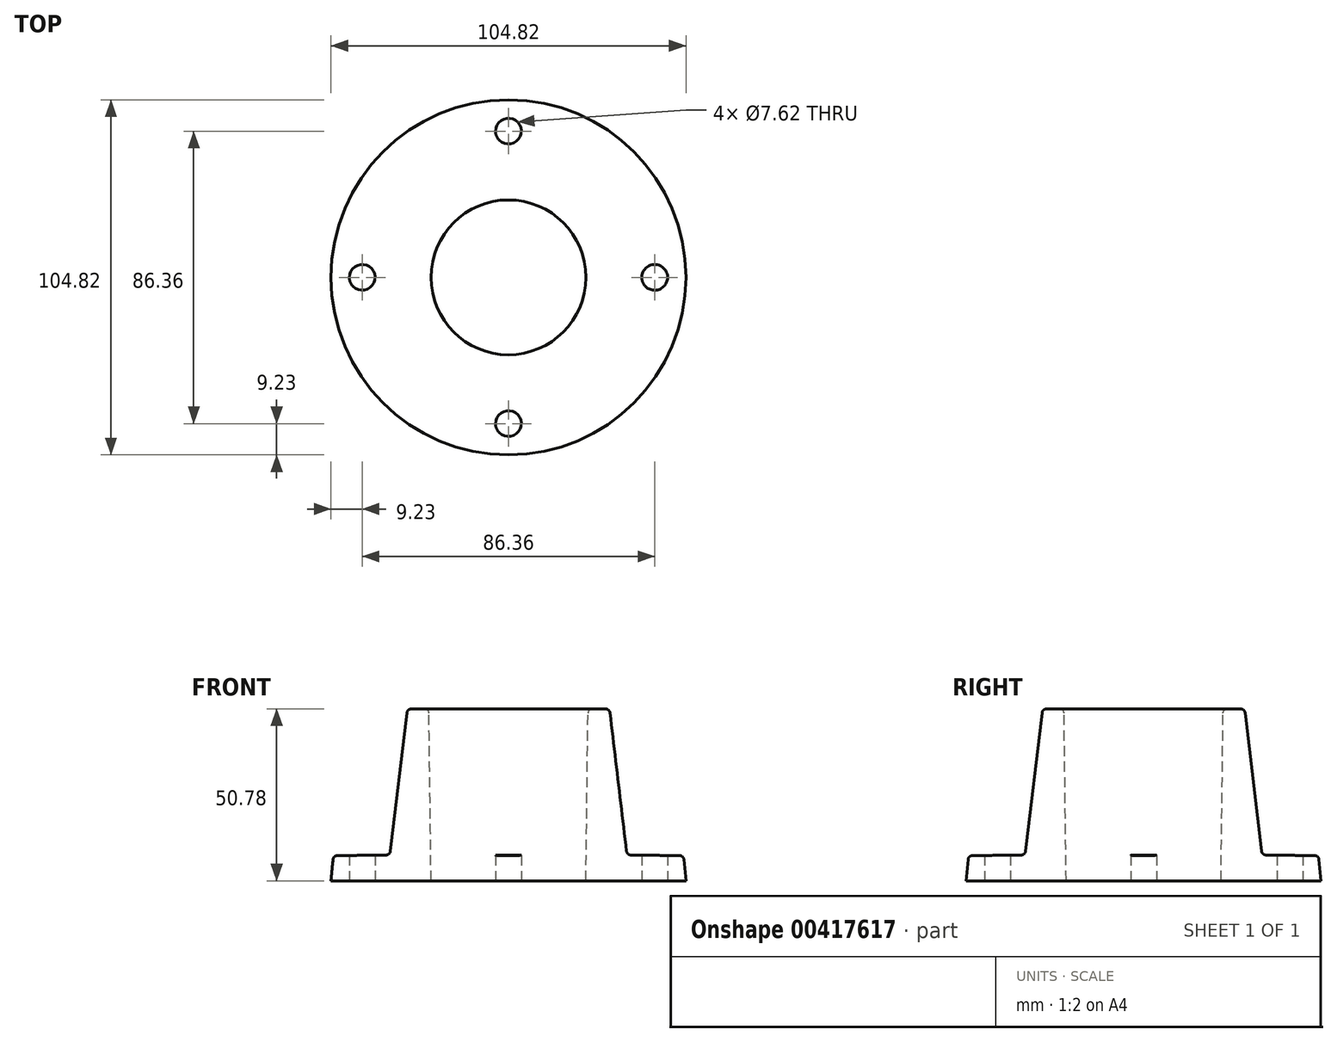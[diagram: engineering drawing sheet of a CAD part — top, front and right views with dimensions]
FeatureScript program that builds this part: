
annotation { "Feature Type Name" : "Feature", "Feature Type Description" : "" }
export const myFeature = defineFeature(function(context is Context, id is Id, definition is map)
    precondition{}
    {
        {
            var Q0;
            Q0=qCreatedBy(makeId("Front.planeOp"),FACE);
            var sketch = newSketch(context, id + "F0", { "sketchPlane" : qUnion([Q0])});
            skLineSegment(sketch, "E0", {"start": v(0, 0) * mm, "end": v(0, 50.8) * mm});
            skLineSegment(sketch, "E1", {"start": v(0, 50.8) * mm, "end": v(23.5, 50.8) * mm});
            skLineSegment(sketch, "E2", {"start": v(0, 0) * mm, "end": v(22.86, 0) * mm});
            skLineSegment(sketch, "E3", {"start": v(22.86, 0) * mm, "end": v(23.5, 50.8) * mm});
            skLineSegment(sketch, "E4", {"start": v(23.5, 50.8) * mm, "end": v(29.84, 50.72) * mm});
            skLineSegment(sketch, "E5", {"start": v(29.84, 50.72) * mm, "end": v(35.9, 0) * mm});
            skLineSegment(sketch, "E6", {"start": v(52.5, 7.41) * mm, "end": v(34.99, 7.63) * mm});
            skLineSegment(sketch, "E7", {"start": v(22.86, 0) * mm, "end": v(35.9, 0) * mm});
            skLineSegment(sketch, "E8", {"start": v(35.9, 0) * mm, "end": v(52.41, 0) * mm});
            skLineSegment(sketch, "E9", {"start": v(52.41, 0) * mm, "end": v(51.7, 7.42) * mm});
            skSolve(sketch);
        }
        {
            var Q0;
            Q0=makeQuery(id+"F0.imprint","IMPRINT",FACE,{"disambiguationData":[TD([[makeQuery(id+"F0.imprint","IMPRINT",EDGE,{"derivedFrom":sQuery(id+"F0.wireOp",EDGE,"E3")}),-1.0]])]});
            var Q1;
            {var subQ0=sQuery(id+"F0.wireOp",EDGE,"E8");Q1=makeQuery(id+"F0.imprint","IMPRINT",FACE,{"disambiguationData":[TD([[makeQuery(id+"F0.imprint","IMPRINT",EDGE,{"derivedFrom":subQ0}),1.0]])]});}
            var Q2;
            Q2=sQuery(id+"F0.wireOp",EDGE,"E0");
            revolve(context, id + "F1", {"entities" : qUnion([Q0, Q1]), "axis" : qUnion([Q2]), "revolveType" : RevolveType.FULL});
        }
        {
            var Q0;
            Q0=makeQuery(id+"F1.opRevolve","SWEPT_FACE",FACE,{"disambiguationData":[OSD([sQuery(id+"F0.wireOp",EDGE,"E7"),sQuery(id+"F0.wireOp",EDGE,"E8")])]});
            var sketch = newSketch(context, id + "F2", { "sketchPlane" : qUnion([Q0])});
            skLineSegment(sketch, "E10", {"start": v(0, 0) * mm, "end": v(0, 43.18) * mm});
            skLineSegment(sketch, "E11", {"start": v(0, 0) * mm, "end": v(43.18, 0) * mm});
            skLineSegment(sketch, "E12", {"start": v(0, 0) * mm, "end": v(0, -43.18) * mm});
            skLineSegment(sketch, "E13", {"start": v(0, 0) * mm, "end": v(-43.18, 0) * mm});
            skCircle(sketch, "E14", {"center": v(0, 43.18) * mm, "radius": 3.81 * mm});
            skCircle(sketch, "E15", {"center": v(43.18, 0) * mm, "radius": 3.81 * mm});
            skCircle(sketch, "E16", {"center": v(0, -43.18) * mm, "radius": 3.81 * mm});
            skCircle(sketch, "E17", {"center": v(-43.18, 0) * mm, "radius": 3.81 * mm});
            skSolve(sketch);
        }
        {
            var Q0;
            Q0 = qSketchRegion(id + "F2", true);
            extrude(context, id + "F3", {"entities" : qUnion([Q0]), "operationType" : NewBodyOperationType.REMOVE, "endBound" : BoundingType.UP_TO_NEXT, "oppositeDirection" : true, "depth" : 25.4 * mm});
        }
        {
            var Q0;
            Q0=makeQuery(id+"F1.opRevolve","SWEPT_EDGE",EDGE,{"disambiguationData":[OSD([sQuery(id+"F0.wireOp",EDGE,"E4"),sQuery(id+"F0.wireOp",EDGE,"E5")])]});
            var Q1;
            Q1=makeQuery(id+"F1.opRevolve","SWEPT_EDGE",EDGE,{"disambiguationData":[OSD([sQuery(id+"F0.wireOp",EDGE,"E1"),sQuery(id+"F0.wireOp",EDGE,"E3"),sQuery(id+"F0.wireOp",EDGE,"E4")])]});
            var Q2;
            Q2=makeQuery(id+"F1.opRevolve","SWEPT_EDGE",EDGE,{"disambiguationData":[OSD([sQuery(id+"F0.wireOp",EDGE,"E5"),sQuery(id+"F0.wireOp",EDGE,"E6")])]});
            var Q3;
            Q3=makeQuery(id+"F1.opRevolve","SWEPT_EDGE",EDGE,{"disambiguationData":[OSD([sQuery(id+"F0.wireOp",EDGE,"E6"),sQuery(id+"F0.wireOp",EDGE,"E9")])]});
            var Q4;
            Q4=makeQuery(id+"F3.boolean.opBoolean","COPY",EDGE,{"derivedFrom":makeQuery(id+"F3.opExtrude","CAP_EDGE",EDGE,{"disambiguationData":[OSD([sQuery(id+"F2.wireOp",EDGE,"E17")])],"isStart":false})});
            var Q5;
            Q5=makeQuery(id+"F3.boolean.opBoolean","COPY",EDGE,{"derivedFrom":makeQuery(id+"F3.opExtrude","CAP_EDGE",EDGE,{"disambiguationData":[OSD([sQuery(id+"F2.wireOp",EDGE,"E14")])],"isStart":false})});
            var Q6;
            Q6=makeQuery(id+"F3.boolean.opBoolean","COPY",EDGE,{"derivedFrom":makeQuery(id+"F3.opExtrude","CAP_EDGE",EDGE,{"disambiguationData":[OSD([sQuery(id+"F2.wireOp",EDGE,"E15")])],"isStart":false})});
            var Q7;
            Q7=makeQuery(id+"F3.boolean.opBoolean","COPY",EDGE,{"derivedFrom":makeQuery(id+"F3.opExtrude","CAP_EDGE",EDGE,{"disambiguationData":[OSD([sQuery(id+"F2.wireOp",EDGE,"E16")])],"isStart":false})});
            fillet(context, id + "F4", {"entities" : qUnion([Q0, Q1, Q2, Q3, Q4, Q5, Q6, Q7]), "radius" : 1.27 * mm, "tangentPropagation" : true, "allowEdgeOverflow" : false});
        }
    });
